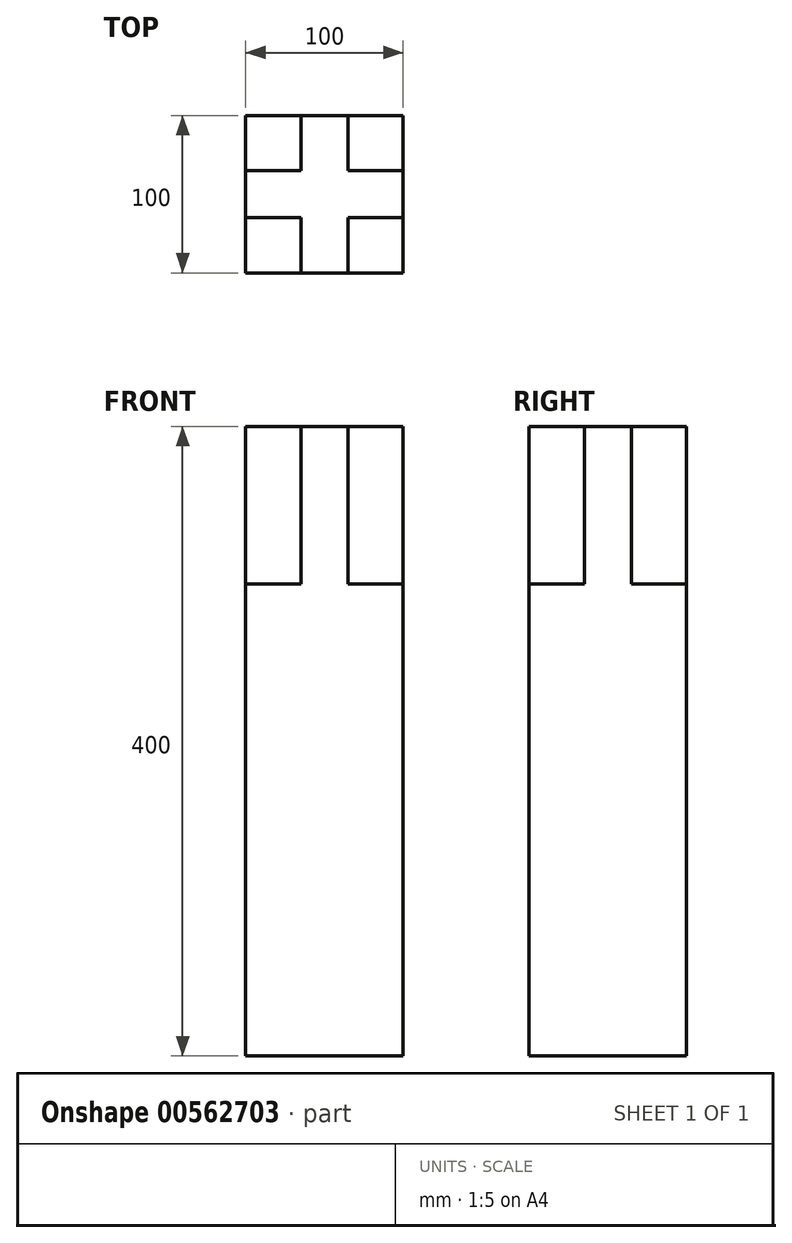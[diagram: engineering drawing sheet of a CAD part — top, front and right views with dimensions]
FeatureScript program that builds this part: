
annotation { "Feature Type Name" : "Feature", "Feature Type Description" : "" }
export const myFeature = defineFeature(function(context is Context, id is Id, definition is map)
    precondition{}
    {
        {
            var Q0;
            Q0=qCreatedBy(makeId("Top.planeOp"),FACE);
            var sketch = newSketch(context, id + "F0", { "sketchPlane" : qUnion([Q0])});
            skLineSegment(sketch, "E0.bottom", {"start": v(50, -50) * mm, "end": v(-50, -50) * mm});
            skLineSegment(sketch, "E0.top", {"start": v(50, 50) * mm, "end": v(-50, 50) * mm});
            skLineSegment(sketch, "E0.left", {"start": v(50, -50) * mm, "end": v(50, 50) * mm});
            skLineSegment(sketch, "E0.right", {"start": v(-50, -50) * mm, "end": v(-50, 50) * mm});
            skPoint(sketch, "E0.middle", {"position": v(0, 0) * mm});
            skSolve(sketch);
        }
        {
            var Q0;
            Q0 = qSketchRegion(id + "F0", true);
            extrude(context, id + "F1", {"entities" : qUnion([Q0]), "depth" : 300 * mm, "offsetDistance" : 25.4 * mm});
        }
        {
            var Q0;
            Q0=makeQuery(id+"F1.opExtrude","CAP_FACE",FACE,{"disambiguationData":[OSD([sQuery(id+"F0.wireOp",EDGE,"E0.bottom"),sQuery(id+"F0.wireOp",EDGE,"E0.top"),sQuery(id+"F0.wireOp",EDGE,"E0.left"),sQuery(id+"F0.wireOp",EDGE,"E0.right")])],"isStart":false});
            var sketch = newSketch(context, id + "F2", { "sketchPlane" : qUnion([Q0])});
            skLineSegment(sketch, "E1.bottom", {"start": v(15, 50) * mm, "end": v(-15, 50) * mm});
            skLineSegment(sketch, "E1.top", {"start": v(15, -50) * mm, "end": v(-15, -50) * mm});
            skLineSegment(sketch, "E1.left", {"start": v(15, 50) * mm, "end": v(15, -50) * mm});
            skLineSegment(sketch, "E1.right", {"start": v(-15, 50) * mm, "end": v(-15, -50) * mm});
            skPoint(sketch, "E1.middle", {"position": v(0, 0) * mm});
            skLineSegment(sketch, "E2.bottom", {"start": v(50, 15) * mm, "end": v(-50, 15) * mm});
            skLineSegment(sketch, "E2.top", {"start": v(50, -15) * mm, "end": v(-50, -15) * mm});
            skLineSegment(sketch, "E2.left", {"start": v(50, 15) * mm, "end": v(50, -15) * mm});
            skLineSegment(sketch, "E2.right", {"start": v(-50, 15) * mm, "end": v(-50, -15) * mm});
            skSolve(sketch);
        }
        {
            var Q0;
            Q0 = qSketchRegion(id + "F2", true);
            extrude(context, id + "F3", {"entities" : qUnion([Q0]), "operationType" : NewBodyOperationType.ADD, "depth" : 100 * mm, "offsetDistance" : 25.4 * mm});
        }
    });
